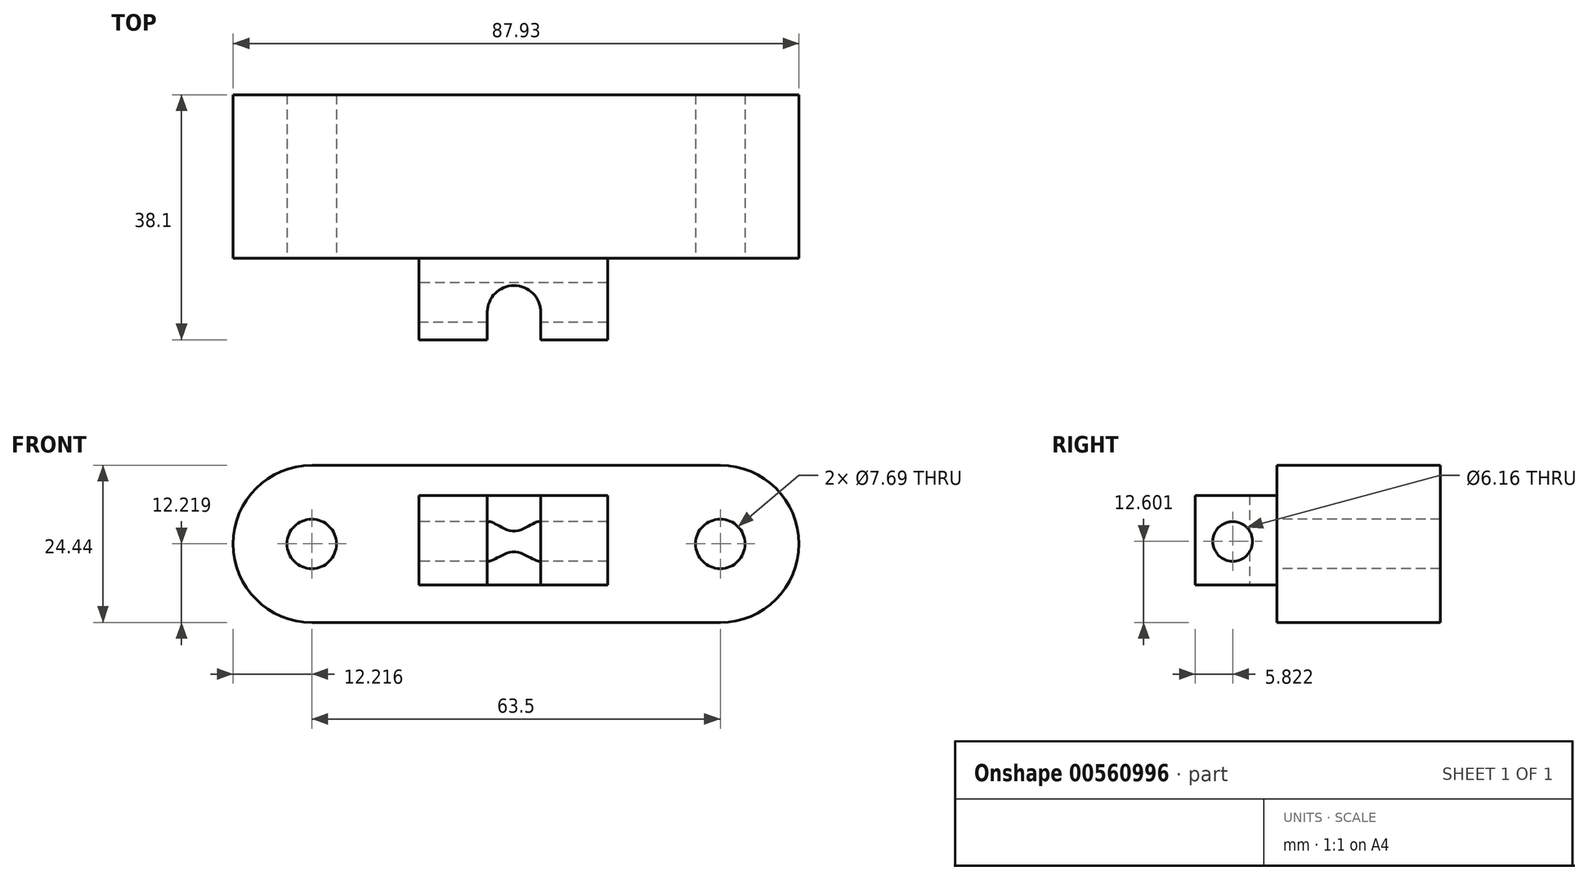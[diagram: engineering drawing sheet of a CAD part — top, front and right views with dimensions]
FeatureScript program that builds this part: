
annotation { "Feature Type Name" : "Feature", "Feature Type Description" : "" }
export const myFeature = defineFeature(function(context is Context, id is Id, definition is map)
    precondition{}
    {
        {
            var Q0;
            Q0=qCreatedBy(makeId("Front.planeOp"),FACE);
            var sketch = newSketch(context, id + "F0", { "sketchPlane" : qUnion([Q0])});
            skLineSegment(sketch, "E0", {"start": v(-28.31, 37.14) * mm, "end": v(35.19, 37.14) * mm});
            skLineSegment(sketch, "E1", {"start": v(-28.31, 12.7) * mm, "end": v(35.19, 12.7) * mm});
            skCircle(sketch, "E2", {"center": v(35.19, 24.92) * mm, "radius": 12.22 * mm});
            skPoint(sketch, "E3.center.orphan", {"position": v(-28.31, 24.92) * mm});
            skCircle(sketch, "E4", {"center": v(-28.31, 24.92) * mm, "radius": 12.22 * mm});
            skSolve(sketch);
        }
        {
            var Q0;
            {var subQ0=sQuery(id+"F0.wireOp",EDGE,"E4");var subQ1=sQuery(id+"F0.wireOp",EDGE,"E0");var subQ2=makeQuery(id+"F0.imprint","INTERSECT",VERTEX,{"disambiguationData":[OD(0.0)],"derivedFrom":[subQ1,subQ0]});Q0=makeQuery(id+"F0.imprint","IMPRINT",FACE,{"disambiguationData":[TD([[makeQuery(id+"F0.imprint","IMPRINT",EDGE,{"disambiguationData":[TD([[subQ2,-1.0]])],"derivedFrom":subQ1}),-1.0]])]});}
            var Q1;
            {var subQ0=sQuery(id+"F0.wireOp",EDGE,"E2");var subQ1=sQuery(id+"F0.wireOp",EDGE,"E0");var subQ2=makeQuery(id+"F0.imprint","INTERSECT",VERTEX,{"derivedFrom":[subQ1,subQ0]});Q1=makeQuery(id+"F0.imprint","IMPRINT",FACE,{"disambiguationData":[TD([[makeQuery(id+"F0.imprint","IMPRINT",EDGE,{"disambiguationData":[TD([[subQ2,1.0]])],"derivedFrom":subQ1}),-1.0]])]});}
            var Q2;
            {var subQ0=sQuery(id+"F0.wireOp",EDGE,"E2");var subQ1=makeQuery(id+"F0.imprint","INTERSECT",VERTEX,{"derivedFrom":[sQuery(id+"F0.wireOp",EDGE,"E0"),subQ0]});Q2=makeQuery(id+"F0.imprint","IMPRINT",FACE,{"disambiguationData":[TD([[makeQuery(id+"F0.imprint","IMPRINT",EDGE,{"disambiguationData":[TD([[subQ1,-1.0]])],"derivedFrom":subQ0}),1.0]])]});}
            extrude(context, id + "F1", {"entities" : qUnion([Q0, Q1, Q2]), "endBound" : BoundingType.SYMMETRIC, "depth" : 25.4 * mm, "offsetDistance" : 25.4 * mm});
        }
        {
            var Q0;
            {var subQ0=sQuery(id+"F0.wireOp",EDGE,"E4");var subQ1=makeQuery(id+"F0.imprint","INTERSECT",VERTEX,{"derivedFrom":[sQuery(id+"F0.wireOp",EDGE,"E0"),subQ0]});Q0=makeQuery(id+"F0.imprint","IMPRINT",FACE,{"disambiguationData":[TD([[makeQuery(id+"F0.imprint","IMPRINT",EDGE,{"disambiguationData":[TD([[subQ1,-1.0]])],"derivedFrom":subQ0}),1.0]])]});}
            var Q1;
            {var subQ0=sQuery(id+"F0.wireOp",EDGE,"E0");Q1=makeQuery(id+"F0.imprint","IMPRINT",FACE,{"disambiguationData":[TD([[makeQuery(id+"F0.imprint","IMPRINT",EDGE,{"derivedFrom":subQ0}),-1.0]])]});}
            var Q2;
            {var subQ0=sQuery(id+"F0.wireOp",EDGE,"E2");var subQ1=makeQuery(id+"F0.imprint","INTERSECT",VERTEX,{"derivedFrom":[sQuery(id+"F0.wireOp",EDGE,"E0"),subQ0]});Q2=makeQuery(id+"F0.imprint","IMPRINT",FACE,{"disambiguationData":[TD([[makeQuery(id+"F0.imprint","IMPRINT",EDGE,{"disambiguationData":[TD([[subQ1,-1.0]])],"derivedFrom":subQ0}),1.0]])]});}
            extrude(context, id + "F2", {"entities" : qUnion([Q0, Q1, Q2]), "operationType" : NewBodyOperationType.ADD, "endBound" : BoundingType.SYMMETRIC, "depth" : 25.4 * mm, "offsetDistance" : 25.4 * mm});
        }
        {
            var Q0;
            {var subQ0=sQuery(id+"F0.wireOp",EDGE,"E4");var subQ1=sQuery(id+"F0.wireOp",EDGE,"E2");var subQ2=sQuery(id+"F0.wireOp",EDGE,"E1");var subQ3=sQuery(id+"F0.wireOp",EDGE,"E0");Q0=makeQuery(id+"F2.boolean.opBoolean","MERGE",FACE,{"derivedFrom":[makeQuery(id+"F1.opExtrude","CAP_FACE",FACE,{"disambiguationData":[OSD([subQ3,subQ2,subQ1,subQ0])],"isStart":false}),makeQuery(id+"F2.opExtrude","CAP_FACE",FACE,{"disambiguationData":[OSD([subQ3,subQ2,subQ1,subQ0])],"isStart":false})]});}
            var sketch = newSketch(context, id + "F3", { "sketchPlane" : qUnion([Q0])});
            skCircle(sketch, "E5", {"center": v(-28.31, 24.92) * mm, "radius": 3.84 * mm});
            skCircle(sketch, "E6", {"center": v(35.19, 24.92) * mm, "radius": 3.84 * mm});
            skSolve(sketch);
        }
        {
            var Q0;
            Q0=makeQuery(id+"F3.imprint","IMPRINT",FACE,{"disambiguationData":[TD([[makeQuery(id+"F3.imprint","IMPRINT",EDGE,{"derivedFrom":sQuery(id+"F3.wireOp",EDGE,"E5")}),1.0]])]});
            var Q1;
            Q1=makeQuery(id+"F3.imprint","IMPRINT",FACE,{"disambiguationData":[TD([[makeQuery(id+"F3.imprint","IMPRINT",EDGE,{"derivedFrom":sQuery(id+"F3.wireOp",EDGE,"E6")}),1.0]])]});
            extrude(context, id + "F4", {"entities" : qUnion([Q0, Q1]), "operationType" : NewBodyOperationType.REMOVE, "endBound" : BoundingType.THROUGH_ALL, "oppositeDirection" : true, "depth" : 25.4 * mm, "offsetDistance" : 25.4 * mm});
        }
        {
            var Q0;
            {var subQ0=sQuery(id+"F0.wireOp",EDGE,"E4");var subQ1=sQuery(id+"F0.wireOp",EDGE,"E2");var subQ2=sQuery(id+"F0.wireOp",EDGE,"E1");var subQ3=sQuery(id+"F0.wireOp",EDGE,"E0");Q0=makeQuery(id+"F2.boolean.opBoolean","MERGE",FACE,{"derivedFrom":[makeQuery(id+"F1.opExtrude","CAP_FACE",FACE,{"disambiguationData":[OSD([subQ3,subQ2,subQ1,subQ0])],"isStart":false}),makeQuery(id+"F2.opExtrude","CAP_FACE",FACE,{"disambiguationData":[OSD([subQ3,subQ2,subQ1,subQ0])],"isStart":false})]});}
            var sketch = newSketch(context, id + "F5", { "sketchPlane" : qUnion([Q0])});
            skLineSegment(sketch, "E7.bottom", {"start": v(17.66, 32.45) * mm, "end": v(-11.67, 32.45) * mm});
            skLineSegment(sketch, "E7.top", {"start": v(17.66, 18.52) * mm, "end": v(-11.67, 18.52) * mm});
            skLineSegment(sketch, "E7.left", {"start": v(17.66, 32.45) * mm, "end": v(17.66, 18.52) * mm});
            skLineSegment(sketch, "E7.right", {"start": v(-11.67, 32.45) * mm, "end": v(-11.67, 18.52) * mm});
            skPoint(sketch, "E7.middle", {"position": v(3, 25.48) * mm});
            skSolve(sketch);
        }
        {
            var Q0;
            Q0=makeQuery(id+"F5.imprint","IMPRINT",FACE,{"disambiguationData":[TD([[makeQuery(id+"F5.imprint","IMPRINT",EDGE,{"derivedFrom":sQuery(id+"F5.wireOp",EDGE,"E7.bottom")}),1.0]])]});
            extrude(context, id + "F6", {"entities" : qUnion([Q0]), "operationType" : NewBodyOperationType.ADD, "depth" : 12.7 * mm, "offsetDistance" : 25.4 * mm});
        }
        {
            var Q0;
            Q0=makeQuery(id+"F6.opExtrude","SWEPT_FACE",FACE,{"disambiguationData":[OSD([sQuery(id+"F5.wireOp",EDGE,"E7.top")])]});
            var sketch = newSketch(context, id + "F7", { "sketchPlane" : qUnion([Q0])});
            skLineSegment(sketch, "E8", {"start": v(7.26, 25.4) * mm, "end": v(7.26, 21.1) * mm});
            skLineSegment(sketch, "E9", {"start": v(-1.03, 25.4) * mm, "end": v(-1.03, 21.1) * mm});
            skArc(sketch, "E10", {"start": v(-1.03, 21.1) * mm, "mid": v(3.12, 16.95) * mm, "end": v(7.26, 21.1) * mm});
            skSolve(sketch);
        }
        {
            var Q0;
            {var subQ0=sQuery(id+"F7.wireOp",EDGE,"E8");Q0=makeQuery(id+"F7.imprint","IMPRINT",FACE,{"disambiguationData":[TD([[makeQuery(id+"F7.imprint","IMPRINT",EDGE,{"derivedFrom":subQ0}),-1.0]])]});}
            extrude(context, id + "F8", {"entities" : qUnion([Q0]), "operationType" : NewBodyOperationType.REMOVE, "endBound" : BoundingType.THROUGH_ALL, "oppositeDirection" : true, "depth" : 25.4 * mm, "offsetDistance" : 25.4 * mm});
        }
        {
            var Q0;
            Q0=makeQuery(id+"F6.opExtrude","SWEPT_FACE",FACE,{"disambiguationData":[OSD([sQuery(id+"F5.wireOp",EDGE,"E7.right")])]});
            var sketch = newSketch(context, id + "F9", { "sketchPlane" : qUnion([Q0])});
            skCircle(sketch, "E11", {"center": v(19.58, 25.3) * mm, "radius": 3.08 * mm});
            skSolve(sketch);
        }
        {
            var Q0;
            Q0=makeQuery(id+"F9.imprint","IMPRINT",FACE,{"disambiguationData":[TD([[makeQuery(id+"F9.imprint","IMPRINT",EDGE,{"derivedFrom":sQuery(id+"F9.wireOp",EDGE,"E11")}),1.0]])]});
            extrude(context, id + "F10", {"entities" : qUnion([Q0]), "operationType" : NewBodyOperationType.REMOVE, "endBound" : BoundingType.THROUGH_ALL, "oppositeDirection" : true, "depth" : 25.4 * mm, "offsetDistance" : 25.4 * mm});
        }
    });
